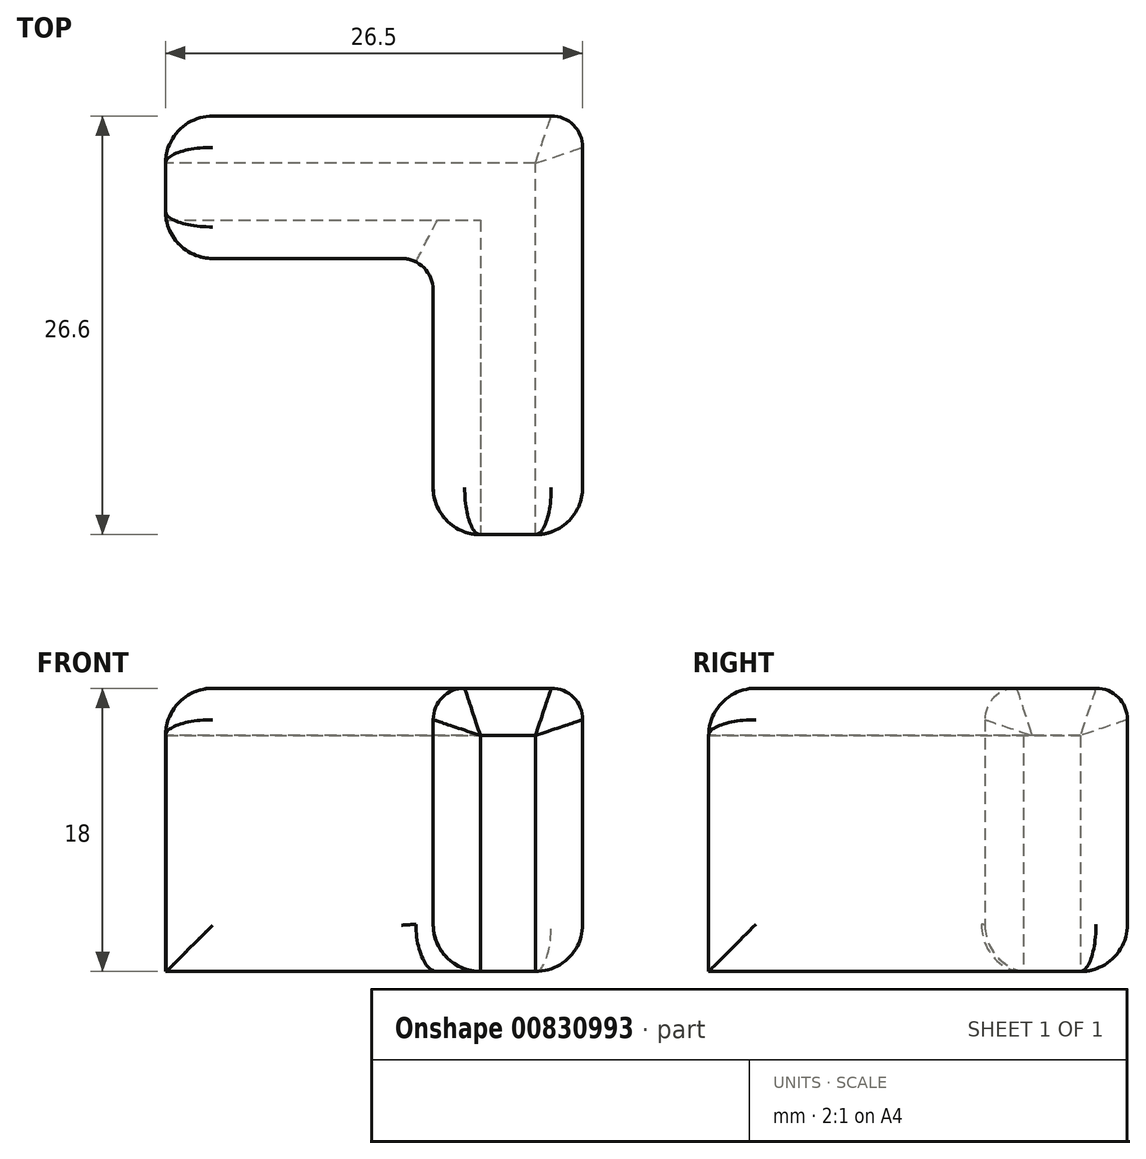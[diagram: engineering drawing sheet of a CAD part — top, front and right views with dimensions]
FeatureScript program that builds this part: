
annotation { "Feature Type Name" : "Feature", "Feature Type Description" : "" }
export const myFeature = defineFeature(function(context is Context, id is Id, definition is map)
    precondition{}
    {
        {
            var Q0;
            Q0=qCreatedBy(makeId("Top.planeOp"),FACE);
            cPlane(context, id + "F0", {"entities" : qUnion([Q0]), "cplaneType" : CPlaneType.OFFSET, "offset" : 10 * mm, "oppositeDirection" : true, "width" : 150 * mm, "height" : 150 * mm});
        }
        {
            var Q0;
            Q0=qCreatedBy(id+"F0.planeOp",FACE);
            var sketch = newSketch(context, id + "F1", { "sketchPlane" : qUnion([Q0])});
            skLineSegment(sketch, "E0", {"start": v(-20, 0) * mm, "end": v(0, 0) * mm});
            skLineSegment(sketch, "E1", {"start": v(0, 0) * mm, "end": v(0, -20) * mm});
            skLineSegment(sketch, "E2", {"start": v(0, -20) * mm, "end": v(3.5, -20) * mm});
            skLineSegment(sketch, "E3", {"start": v(3.5, -20) * mm, "end": v(3.5, 3.6) * mm});
            skLineSegment(sketch, "E4", {"start": v(3.5, 3.6) * mm, "end": v(-20, 3.6) * mm});
            skLineSegment(sketch, "E5", {"start": v(-20, 3.6) * mm, "end": v(-20, 0) * mm});
            skLineSegment(sketch, "E6", {"start": v(-20, 3.6) * mm, "end": v(-20, 6.6) * mm});
            skLineSegment(sketch, "E7", {"start": v(-20, 6.6) * mm, "end": v(6.5, 6.6) * mm});
            skLineSegment(sketch, "E8", {"start": v(6.5, 6.6) * mm, "end": v(6.5, -20) * mm});
            skLineSegment(sketch, "E9", {"start": v(6.5, -20) * mm, "end": v(-3, -20) * mm});
            skLineSegment(sketch, "E10", {"start": v(-3, -20) * mm, "end": v(-3, -2.45) * mm});
            skLineSegment(sketch, "E11", {"start": v(-3, -2.45) * mm, "end": v(-20, -2.45) * mm});
            skLineSegment(sketch, "E12", {"start": v(-20, -2.45) * mm, "end": v(-20, 0) * mm});
            skSolve(sketch);
        }
        {
            var Q0;
            Q0 = qSketchRegion(id + "F1", true);
            extrude(context, id + "F2", {"entities" : qUnion([Q0]), "depth" : 18 * mm, "offsetDistance" : 25 * mm});
        }
        {
            var Q0;
            Q0=makeQuery(id+"F1.imprint","IMPRINT",FACE,{"disambiguationData":[TD([[makeQuery(id+"F1.imprint","IMPRINT",EDGE,{"derivedFrom":sQuery(id+"F1.wireOp",EDGE,"E0")}),1.0]])]});
            extrude(context, id + "F3", {"entities" : qUnion([Q0]), "operationType" : NewBodyOperationType.REMOVE, "depth" : 15 * mm, "offsetDistance" : 25 * mm});
        }
        {
            var Q0;
            Q0=makeQuery(id+"F2.opExtrude","SWEPT_EDGE",EDGE,{"disambiguationData":[OSD([sQuery(id+"F1.wireOp",EDGE,"E7"),sQuery(id+"F1.wireOp",EDGE,"E8")])]});
            var Q1;
            Q1=makeQuery(id+"F2.opExtrude","CAP_EDGE",EDGE,{"disambiguationData":[OSD([sQuery(id+"F1.wireOp",EDGE,"E8")])],"isStart":false});
            var Q2;
            Q2=makeQuery(id+"F2.opExtrude","CAP_EDGE",EDGE,{"disambiguationData":[OSD([sQuery(id+"F1.wireOp",EDGE,"E7")])],"isStart":false});
            var Q3;
            Q3=makeQuery(id+"F2.opExtrude","CAP_EDGE",EDGE,{"disambiguationData":[OSD([sQuery(id+"F1.wireOp",EDGE,"E10")])],"isStart":false});
            var Q4;
            Q4=makeQuery(id+"F2.opExtrude","CAP_EDGE",EDGE,{"disambiguationData":[OSD([sQuery(id+"F1.wireOp",EDGE,"E11")])],"isStart":false});
            var Q5;
            Q5=makeQuery(id+"F2.opExtrude","SWEPT_EDGE",EDGE,{"disambiguationData":[OSD([sQuery(id+"F1.wireOp",EDGE,"E10"),sQuery(id+"F1.wireOp",EDGE,"E11")])]});
            fillet(context, id + "F4", {"entities" : qUnion([Q0, Q1, Q2, Q3, Q4, Q5]), "radius" : 2 * mm, "tangentPropagation" : true, "allowEdgeOverflow" : false});
        }
        {
            var Q0;
            Q0=makeQuery(id+"F2.opExtrude","SWEPT_EDGE",EDGE,{"disambiguationData":[OSD([sQuery(id+"F1.wireOp",EDGE,"E8"),sQuery(id+"F1.wireOp",EDGE,"E9")])]});
            var Q1;
            Q1=makeQuery(id+"F2.opExtrude","CAP_EDGE",EDGE,{"disambiguationData":[OSD([sQuery(id+"F1.wireOp",EDGE,"E5"),sQuery(id+"F1.wireOp",EDGE,"E6"),sQuery(id+"F1.wireOp",EDGE,"E12")])],"isStart":false});
            var Q2;
            Q2=makeQuery(id+"F2.opExtrude","CAP_EDGE",EDGE,{"disambiguationData":[OSD([sQuery(id+"F1.wireOp",EDGE,"E7")])],"isStart":true});
            var Q3;
            Q3=makeQuery(id+"F2.opExtrude","CAP_EDGE",EDGE,{"disambiguationData":[OSD([sQuery(id+"F1.wireOp",EDGE,"E11")])],"isStart":true});
            fillet(context, id + "F5", {"entities" : qUnion([Q0, Q1, Q2, Q3]), "radius" : 3 * mm, "tangentPropagation" : true, "allowEdgeOverflow" : false});
        }
    });
